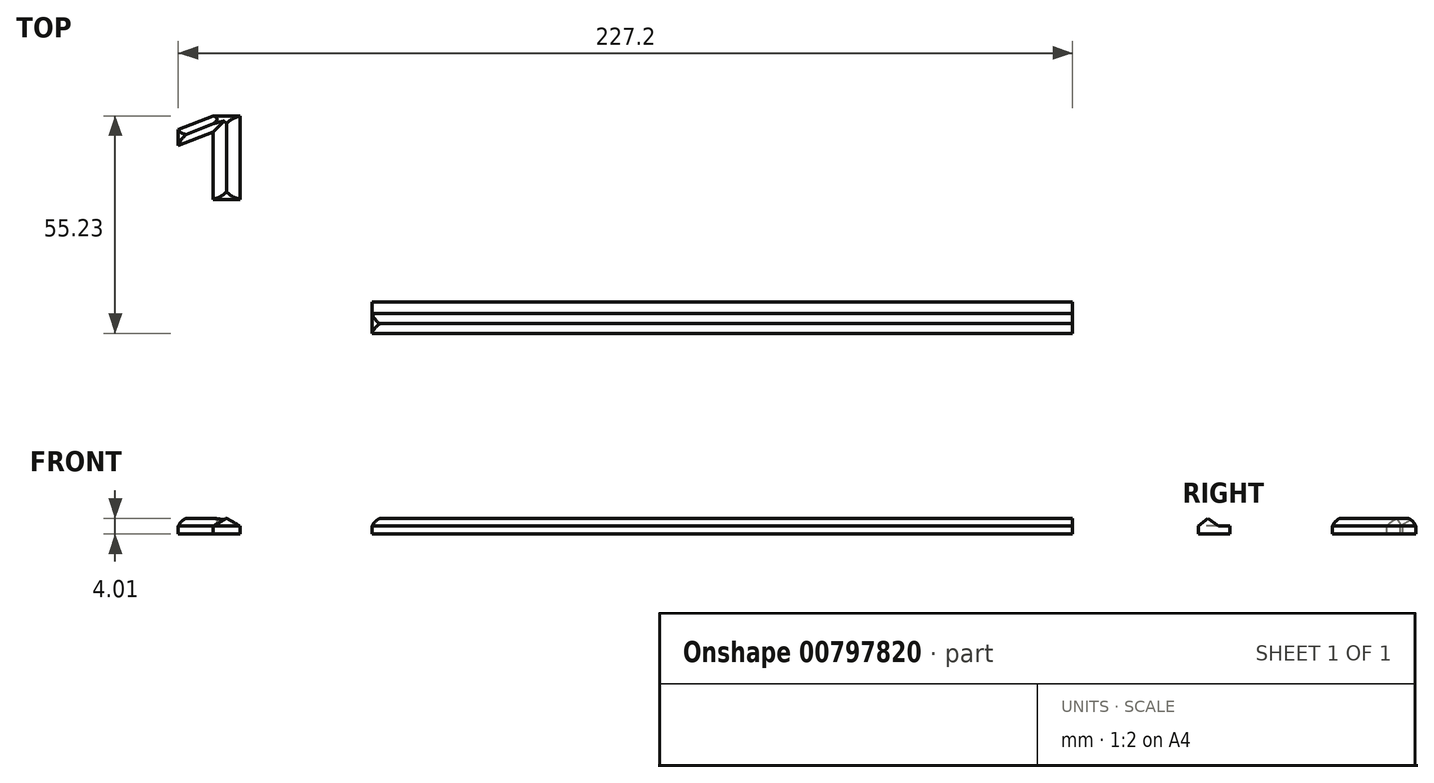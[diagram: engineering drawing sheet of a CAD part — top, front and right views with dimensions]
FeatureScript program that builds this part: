
annotation { "Feature Type Name" : "Feature", "Feature Type Description" : "" }
export const myFeature = defineFeature(function(context is Context, id is Id, definition is map)
    precondition{}
    {
        {
            var Q0;
            Q0=qCreatedBy(makeId("Right.planeOp"),FACE);
            var sketch = newSketch(context, id + "F0", { "sketchPlane" : qUnion([Q0])});
            skLineSegment(sketch, "E0", {"start": v(0, 0) * mm, "end": v(-8, 0) * mm});
            skLineSegment(sketch, "E1", {"start": v(-8, 0) * mm, "end": v(-8, 2) * mm});
            skLineSegment(sketch, "E2", {"start": v(-8, 2) * mm, "end": v(-5.58, 4) * mm});
            skLineSegment(sketch, "E3", {"start": v(-5.58, 4) * mm, "end": v(-3, 2) * mm});
            skLineSegment(sketch, "E4", {"start": v(-3, 2) * mm, "end": v(0, 2) * mm});
            skLineSegment(sketch, "E5", {"start": v(0, 2) * mm, "end": v(0, 0) * mm});
            skSolve(sketch);
        }
        {
            var Q0;
            Q0=makeQuery(id+"F0.imprint","IMPRINT",FACE,{"disambiguationData":[TD([[makeQuery(id+"F0.imprint","IMPRINT",EDGE,{"derivedFrom":sQuery(id+"F0.wireOp",EDGE,"E0")}),-1.0]])]});
            extrude(context, id + "F1", {"entities" : qUnion([Q0]), "depth" : 178 * mm, "offsetDistance" : 25 * mm});
        }
        {
            var Q0;
            Q0=makeQuery(id+"F1.opExtrude","SWEPT_FACE",FACE,{"disambiguationData":[OSD([sQuery(id+"F0.wireOp",EDGE,"E1")])]});
            var sketch = newSketch(context, id + "F2", { "sketchPlane" : qUnion([Q0])});
            skPoint(sketch, "E6", {"position": v(2, 4) * mm});
            skPoint(sketch, "E7", {"position": v(0, 2) * mm});
            skArc(sketch, "E8", {"start": v(2, 4) * mm, "mid": v(0.85, 3.15) * mm, "end": v(0, 2) * mm});
            skLineSegment(sketch, "E9", {"start": v(2, 4) * mm, "end": v(0, 4) * mm});
            skLineSegment(sketch, "E10", {"start": v(0, 4) * mm, "end": v(0, 2) * mm});
            skLineSegment(sketch, "E11", {"start": v(89, 6.76) * mm, "end": v(89, -3.8) * mm, "construction": true});
            skPoint(sketch, "E11.startSnap0", {"position": v(89, 2) * mm});
            skPoint(sketch, "E12.MirrorP", {"position": v(176, 4) * mm});
            skPoint(sketch, "E13.MirrorP", {"position": v(178, 2) * mm});
            skArc(sketch, "E14.MirrorCS", {"start": v(176, 4) * mm, "mid": v(177.15, 3.15) * mm, "end": v(178, 2) * mm});
            skLineSegment(sketch, "E15.MirrorCS", {"start": v(176, 4) * mm, "end": v(178, 4) * mm});
            skLineSegment(sketch, "E16.MirrorCS", {"start": v(178, 4) * mm, "end": v(178, 2) * mm});
            skSolve(sketch);
        }
        {
            var Q0;
            Q0=makeQuery(id+"F2.imprint","IMPRINT",FACE,{"disambiguationData":[TD([[makeQuery(id+"F2.imprint","IMPRINT",EDGE,{"derivedFrom":sQuery(id+"F2.wireOp",EDGE,"E8")}),-1.0]])]});
            var Q1;
            Q1=makeQuery(id+"F2.imprint","IMPRINT",FACE,{"disambiguationData":[TD([[makeQuery(id+"F2.imprint","IMPRINT",EDGE,{"derivedFrom":sQuery(id+"F2.wireOp",EDGE,"E14.MirrorCS")}),1.0]])]});
            var Q2;
            Q2=makeQuery(id+"F1.opExtrude","SWEPT_FACE",FACE,{"disambiguationData":[OSD([sQuery(id+"F0.wireOp",EDGE,"E5")])]});
            extrude(context, id + "F3", {"entities" : qUnion([Q0, Q1]), "operationType" : NewBodyOperationType.REMOVE, "endBound" : BoundingType.UP_TO_SURFACE, "oppositeDirection" : true, "depth" : 25 * mm, "endBoundEntityFace" : qUnion([Q2]), "offsetDistance" : 25 * mm});
        }
        {
            var Q0;
            Q0=qCreatedBy(makeId("Top.planeOp"),FACE);
            var sketch = newSketch(context, id + "F4", { "sketchPlane" : qUnion([Q0])});
            skLineSegment(sketch, "E17.bottom", {"start": v(-40.4, 47.23) * mm, "end": v(-33.48, 47.23) * mm});
            skLineSegment(sketch, "E17.top", {"start": v(-40.4, 26.01) * mm, "end": v(-33.48, 26.01) * mm});
            skLineSegment(sketch, "E17.left", {"start": v(-40.4, 43.15) * mm, "end": v(-40.4, 26.01) * mm});
            skLineSegment(sketch, "E17.right", {"start": v(-33.48, 47.23) * mm, "end": v(-33.48, 26.01) * mm});
            skLineSegment(sketch, "E18", {"start": v(-40.4, 47.23) * mm, "end": v(-49.2, 43.78) * mm});
            skLineSegment(sketch, "E19", {"start": v(-49.2, 43.78) * mm, "end": v(-49.2, 39.69) * mm});
            skLineSegment(sketch, "E20", {"start": v(-49.2, 39.69) * mm, "end": v(-40.4, 43.15) * mm});
            skSolve(sketch);
        }
        {
            var Q0;
            Q0=makeQuery(id+"F4.imprint","IMPRINT",FACE,{"disambiguationData":[TD([[makeQuery(id+"F4.imprint","IMPRINT",EDGE,{"derivedFrom":sQuery(id+"F4.wireOp",EDGE,"E17.bottom")}),-1.0]])]});
            extrude(context, id + "F5", {"entities" : qUnion([Q0]), "depth" : 2 * mm, "offsetDistance" : 25 * mm});
        }
        {
            var Q0;
            Q0=makeQuery(id+"F5.opExtrude","CAP_FACE",FACE,{"disambiguationData":[OSD([sQuery(id+"F4.wireOp",EDGE,"E17.bottom"),sQuery(id+"F4.wireOp",EDGE,"E17.top"),sQuery(id+"F4.wireOp",EDGE,"E17.left"),sQuery(id+"F4.wireOp",EDGE,"E17.right"),sQuery(id+"F4.wireOp",EDGE,"E18"),sQuery(id+"F4.wireOp",EDGE,"E19"),sQuery(id+"F4.wireOp",EDGE,"E20")])],"isStart":false});
            cPlane(context, id + "F6", {"entities" : qUnion([Q0]), "cplaneType" : CPlaneType.OFFSET, "offset" : 2 * mm, "width" : 150 * mm, "height" : 150 * mm});
        }
        {
            var Q0;
            Q0=qCreatedBy(id+"F6.planeOp",FACE);
            var sketch = newSketch(context, id + "F7", { "sketchPlane" : qUnion([Q0])});
            skLineSegment(sketch, "E21", {"start": v(-49.2, 43.78) * mm, "end": v(-49.2, 39.69) * mm, "construction": true});
            skLineSegment(sketch, "E22", {"start": v(-40.4, 47.23) * mm, "end": v(-40.4, 43.15) * mm, "construction": true});
            skLineSegment(sketch, "E23", {"start": v(-40.4, 47.23) * mm, "end": v(-33.48, 47.23) * mm, "construction": true});
            skLineSegment(sketch, "E24", {"start": v(-40.4, 26.01) * mm, "end": v(-33.48, 26.01) * mm, "construction": true});
            skPoint(sketch, "E25", {"position": v(-49.2, 41.73) * mm});
            skPoint(sketch, "E26", {"position": v(-40.4, 45.2) * mm});
            skPoint(sketch, "E27", {"position": v(-36.94, 47.23) * mm});
            skPoint(sketch, "E28", {"position": v(-36.94, 26.01) * mm});
            skLineSegment(sketch, "E29", {"start": v(-49.2, 41.73) * mm, "end": v(-36.94, 46.55) * mm});
            skLineSegment(sketch, "E30", {"start": v(-36.94, 47.23) * mm, "end": v(-36.94, 26.01) * mm});
            skSolve(sketch);
        }
        {
            var Q0;
            Q0=makeQuery(id+"F5.opExtrude","SWEPT_FACE",FACE,{"disambiguationData":[OSD([sQuery(id+"F4.wireOp",EDGE,"E19")])]});
            var sketch = newSketch(context, id + "F8", { "sketchPlane" : qUnion([Q0])});
            skLineSegment(sketch, "E31", {"start": v(-43.78, 2) * mm, "end": v(-39.69, 2) * mm});
            skLineSegment(sketch, "E32", {"start": v(-39.69, 2) * mm, "end": v(-41.75, 4) * mm});
            skLineSegment(sketch, "E33", {"start": v(-41.75, 4) * mm, "end": v(-43.78, 2) * mm});
            skSolve(sketch);
        }
        {
            var Q0;
            Q0=makeQuery(id+"F8.imprint","IMPRINT",FACE,{"disambiguationData":[TD([[makeQuery(id+"F8.imprint","IMPRINT",EDGE,{"derivedFrom":sQuery(id+"F8.wireOp",EDGE,"E31")}),1.0]])]});
            var Q1;
            Q1=sQuery(id+"F7.wireOp",EDGE,"E29");
            sweep(context, id + "F9", {"operationType" : NewBodyOperationType.ADD, "profiles" : qUnion([Q0]), "path" : qUnion([Q1])});
        }
        {
            var Q0;
            Q0=makeQuery(id+"F5.opExtrude","SWEPT_FACE",FACE,{"disambiguationData":[OSD([sQuery(id+"F4.wireOp",EDGE,"E17.top")])]});
            var sketch = newSketch(context, id + "F10", { "sketchPlane" : qUnion([Q0])});
            skLineSegment(sketch, "E34", {"start": v(-40.4, 2) * mm, "end": v(-33.48, 2) * mm});
            skLineSegment(sketch, "E35", {"start": v(-33.48, 2) * mm, "end": v(-36.96, 4) * mm});
            skLineSegment(sketch, "E36", {"start": v(-36.96, 4) * mm, "end": v(-40.4, 2) * mm});
            skPoint(sketch, "E37", {"position": v(-47.2, 4) * mm});
            skPoint(sketch, "E38", {"position": v(-49.2, 2) * mm});
            skArc(sketch, "E39", {"start": v(-47.2, 4) * mm, "mid": v(-48.39, 3.2) * mm, "end": v(-49.2, 2) * mm});
            skLineSegment(sketch, "E40", {"start": v(-47.2, 4) * mm, "end": v(-49.2, 4) * mm});
            skLineSegment(sketch, "E41", {"start": v(-49.2, 4) * mm, "end": v(-49.2, 2) * mm});
            skSolve(sketch);
        }
        {
            var Q0;
            Q0=makeQuery(id+"F10.imprint","IMPRINT",FACE,{"disambiguationData":[TD([[makeQuery(id+"F10.imprint","IMPRINT",EDGE,{"derivedFrom":sQuery(id+"F10.wireOp",EDGE,"E34")}),1.0]])]});
            var Q1;
            Q1=sQuery(id+"F7.wireOp",EDGE,"E30");
            sweep(context, id + "F11", {"operationType" : NewBodyOperationType.ADD, "profiles" : qUnion([Q0]), "path" : qUnion([Q1])});
        }
        {
            var Q0;
            Q0=makeQuery(id+"F10.imprint","IMPRINT",FACE,{"disambiguationData":[TD([[makeQuery(id+"F10.imprint","IMPRINT",EDGE,{"derivedFrom":sQuery(id+"F10.wireOp",EDGE,"E39")}),-1.0]])]});
            var Q1;
            Q1=makeQuery(id+"F5.opExtrude","SWEPT_FACE",FACE,{"disambiguationData":[OSD([sQuery(id+"F4.wireOp",EDGE,"E18")])]});
            extrude(context, id + "F12", {"entities" : qUnion([Q0]), "operationType" : NewBodyOperationType.REMOVE, "endBound" : BoundingType.UP_TO_SURFACE, "oppositeDirection" : true, "depth" : 25 * mm, "endBoundEntityFace" : qUnion([Q1]), "offsetDistance" : 25 * mm});
        }
        {
            var Q0;
            Q0=makeQuery(id+"F5.opExtrude","SWEPT_FACE",FACE,{"disambiguationData":[OSD([sQuery(id+"F4.wireOp",EDGE,"E17.right")])]});
            var sketch = newSketch(context, id + "F13", { "sketchPlane" : qUnion([Q0])});
            skPoint(sketch, "E42", {"position": v(28.01, 4) * mm});
            skPoint(sketch, "E43", {"position": v(26.01, 2) * mm});
            skPoint(sketch, "E44", {"position": v(45.23, 4) * mm});
            skPoint(sketch, "E45", {"position": v(47.23, 2) * mm});
            skArc(sketch, "E46", {"start": v(28.01, 4) * mm, "mid": v(26.82, 3.2) * mm, "end": v(26.01, 2) * mm});
            skLineSegment(sketch, "E47", {"start": v(28.01, 4) * mm, "end": v(26.01, 4) * mm});
            skLineSegment(sketch, "E48", {"start": v(26.01, 4) * mm, "end": v(26.01, 2) * mm});
            skLineSegment(sketch, "E49", {"start": v(45.23, 4) * mm, "end": v(48.9, 4) * mm});
            skLineSegment(sketch, "E50", {"start": v(48.9, 4) * mm, "end": v(48.9, 2) * mm});
            skLineSegment(sketch, "E51", {"start": v(48.9, 2) * mm, "end": v(47.23, 2) * mm});
            skArc(sketch, "E52", {"start": v(47.23, 2) * mm, "mid": v(46.43, 3.2) * mm, "end": v(45.23, 4) * mm});
            skSolve(sketch);
        }
        {
            var Q0;
            Q0=makeQuery(id+"F13.imprint","IMPRINT",FACE,{"disambiguationData":[TD([[makeQuery(id+"F13.imprint","IMPRINT",EDGE,{"derivedFrom":sQuery(id+"F13.wireOp",EDGE,"E46")}),-1.0]])]});
            var Q1;
            Q1=makeQuery(id+"F13.imprint","IMPRINT",FACE,{"disambiguationData":[TD([[makeQuery(id+"F13.imprint","IMPRINT",EDGE,{"derivedFrom":sQuery(id+"F13.wireOp",EDGE,"E49")}),-1.0]])]});
            var Q2;
            Q2=makeQuery(id+"F9.boolean.opBoolean","MERGE",FACE,{"derivedFrom":[makeQuery(id+"F5.opExtrude","SWEPT_FACE",FACE,{"disambiguationData":[OSD([sQuery(id+"F4.wireOp",EDGE,"E19")])]}),makeQuery(id+"F9.opSweep","CAP_FACE",FACE,{"disambiguationData":[OSD([sQuery(id+"F7.wireOp",VERTEX,"E29.start"),sQuery(id+"F8.wireOp",EDGE,"E31"),sQuery(id+"F8.wireOp",EDGE,"E32"),sQuery(id+"F8.wireOp",EDGE,"E33")])],"isStart":true})]});
            extrude(context, id + "F14", {"entities" : qUnion([Q0, Q1]), "operationType" : NewBodyOperationType.REMOVE, "endBound" : BoundingType.UP_TO_SURFACE, "oppositeDirection" : true, "depth" : 25 * mm, "endBoundEntityFace" : qUnion([Q2]), "offsetDistance" : 25 * mm});
        }
    });
